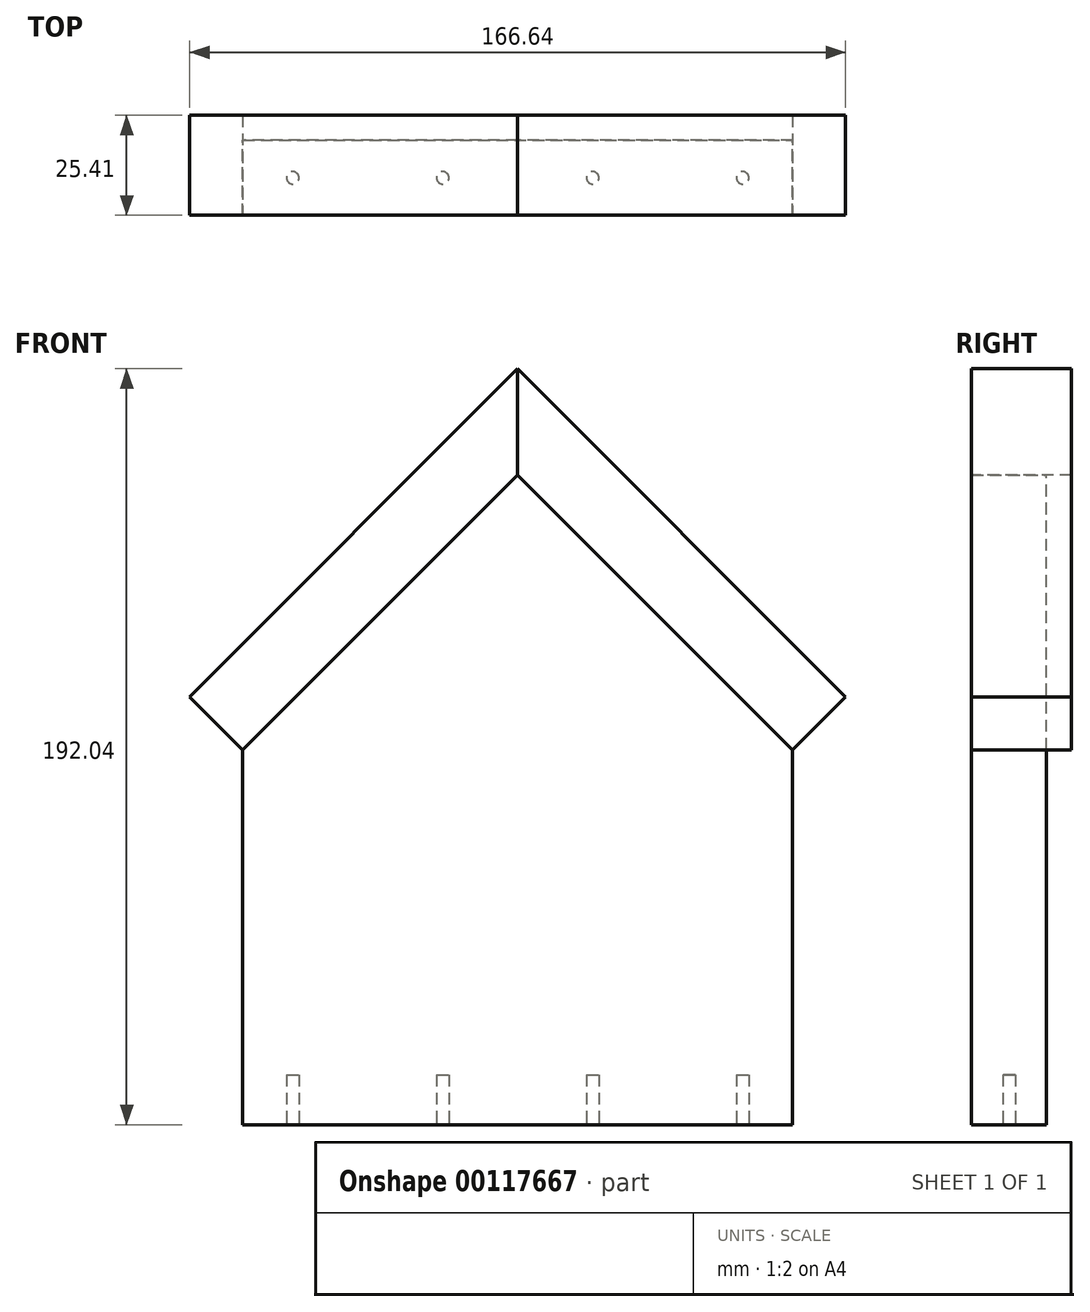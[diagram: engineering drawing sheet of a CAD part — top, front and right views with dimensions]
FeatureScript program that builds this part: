
annotation { "Feature Type Name" : "Feature", "Feature Type Description" : "" }
export const myFeature = defineFeature(function(context is Context, id is Id, definition is map)
    precondition{}
    {
        {
            var Q0;
            Q0=qCreatedBy(makeId("Front.planeOp"),FACE);
            var sketch = newSketch(context, id + "F0", { "sketchPlane" : qUnion([Q0])});
            skLineSegment(sketch, "E0", {"start": v(-69.85, 0) * mm, "end": v(69.85, 0) * mm});
            skLineSegment(sketch, "E1", {"start": v(69.85, 0) * mm, "end": v(69.85, 95.25) * mm});
            skLineSegment(sketch, "E2", {"start": v(69.85, 95.25) * mm, "end": v(0, 165.1) * mm});
            skLineSegment(sketch, "E3", {"start": v(0, 165.1) * mm, "end": v(-69.85, 95.25) * mm});
            skLineSegment(sketch, "E4", {"start": v(-69.85, 95.25) * mm, "end": v(-69.85, 0) * mm});
            skSolve(sketch);
        }
        {
            var Q0;
            Q0 = qSketchRegion(id + "F0", true);
            extrude(context, id + "F1", {"entities" : qUnion([Q0]), "endBound" : BoundingType.SYMMETRIC, "depth" : 19.05 * mm});
        }
        {
            var Q0;
            Q0=makeQuery(id+"F1.opExtrude","CAP_FACE",FACE,{"disambiguationData":[OSD([sQuery(id+"F0.wireOp",EDGE,"E0"),sQuery(id+"F0.wireOp",EDGE,"E1"),sQuery(id+"F0.wireOp",EDGE,"E2"),sQuery(id+"F0.wireOp",EDGE,"E3"),sQuery(id+"F0.wireOp",EDGE,"E4")])],"isStart":false});
            var sketch = newSketch(context, id + "F2", { "sketchPlane" : qUnion([Q0])});
            skLineSegment(sketch, "E5", {"start": v(-69.85, 95.25) * mm, "end": v(0, 165.1) * mm});
            skLineSegment(sketch, "E6", {"start": v(-69.85, 95.25) * mm, "end": v(-83.32, 108.72) * mm});
            skLineSegment(sketch, "E7", {"start": v(-83.32, 108.72) * mm, "end": v(0, 192.04) * mm});
            skLineSegment(sketch, "E8", {"start": v(0, 192.04) * mm, "end": v(0, 165.1) * mm});
            skSolve(sketch);
        }
        {
            var Q0;
            Q0 = qSketchRegion(id + "F2", true);
            extrude(context, id + "F3", {"entities" : qUnion([Q0]), "oppositeDirection" : true, "depth" : 25.4 * mm});
        }
        {
            var Q0;
            Q0=makeQuery(id+"F3.opExtrude","SWEPT_BODY",BODY,{"disambiguationData":[OSD([sQuery(id+"F2.wireOp",EDGE,"E5"),sQuery(id+"F2.wireOp",EDGE,"E6"),sQuery(id+"F2.wireOp",EDGE,"E7"),sQuery(id+"F2.wireOp",EDGE,"E8")])]});
            var Q1;
            Q1=qCreatedBy(makeId("Right.planeOp"),FACE);
            mirror(context, id + "F4", {"entities" : qUnion([Q0]), "mirrorPlane" : qUnion([Q1])});
        }
        {
            var Q0;
            Q0=makeQuery(id+"F1.opExtrude","SWEPT_FACE",FACE,{"disambiguationData":[OSD([sQuery(id+"F0.wireOp",EDGE,"E0")])]});
            var sketch = newSketch(context, id + "F5", { "sketchPlane" : qUnion([Q0])});
            skLineSegment(sketch, "E9", {"start": v(69.85, 0) * mm, "end": v(57.15, 0) * mm});
            skPoint(sketch, "E9.endSnap0", {"position": v(69.85, 0) * mm});
            skLineSegment(sketch, "E10", {"start": v(57.15, 0) * mm, "end": v(19.05, 0) * mm});
            skLineSegment(sketch, "E11", {"start": v(19.05, 0) * mm, "end": v(-19.05, 0) * mm});
            skLineSegment(sketch, "E12", {"start": v(-19.05, 0) * mm, "end": v(-57.15, 0) * mm});
            skLineSegment(sketch, "E13", {"start": v(-57.15, 0) * mm, "end": v(-69.85, 0) * mm});
            skPoint(sketch, "E13.endSnap0", {"position": v(-69.85, 0) * mm});
            skCircle(sketch, "E14", {"center": v(57.15, 0) * mm, "radius": 1.59 * mm});
            skCircle(sketch, "E15", {"center": v(19.05, 0) * mm, "radius": 1.59 * mm});
            skCircle(sketch, "E16", {"center": v(-19.05, 0) * mm, "radius": 1.59 * mm});
            skCircle(sketch, "E17", {"center": v(-57.15, 0) * mm, "radius": 1.59 * mm});
            skSolve(sketch);
        }
        {
            var Q0;
            Q0 = qSketchRegion(id + "F5", true);
            extrude(context, id + "F6", {"entities" : qUnion([Q0]), "operationType" : NewBodyOperationType.REMOVE, "oppositeDirection" : true, "depth" : 12.7 * mm});
        }
    });
